# Revit family: Hager-Orion_Plus-IP65-D250-Cl.I-Steel_encl-630A-NoHosted-BE-en
name_source: partatom
category: Electrical Equipment
units: mm (PartAtom-declared; Revit-internal decimal feet)

## family parameters
Always vertical = Yes
Cut with Voids When Loaded = No
Panel Configuration = Two Columns, Circuits Across
Part Type = Panelboard
Room Calculation Point = No
Round Connector Dimension = Use Diameter
Shared = No
Work Plane-Based = Yes

## types (10) — shared parameters
Default Elevation = 1219 mm
EF000003 - Mounting method = EV000384 - Surface mounted (plaster)
EF000007 - Colour = EV000270 - Grey
EF000049 - Depth = 250 mm  [stored 0.82021 ft]
EF000116 - RAL-number = 7035
EF000118 - With mounting plate = No
EF000437 - Number of conduit inlets = 2
EF001088 - Extension possible = Yes
EF001596 - Material housing = EV000179 - Steel
EF001613 - Circuit integrity = EV000494 - None
EF004293 - Impact strength = EV008784 - IK10
EF004464 - Type of door = EV002646 - Single
EF005474 - Degree of protection (IP) = EV006421 - IP65
EF006306 - With lock = Yes
EF007800 - Suitable for lightning protection = No
EF008873 - Nominal current (In) = 630 A
EF009171 - Material plate thickness door/cover = 2 mm  [stored 0.00656168 ft]
EF009212 - Cover model = EV000116 - Closed
EF009554 - Number of openings for flange plates = 2
EF015940 - Cover with overpressure release = No
HG000002 - With door or cover = Yes
HG000003 - Range = Orion Plus
HG000006 - Flush mounted = No
HG000009 - Double swing door = No
HG000010 - Asymmetric doors = No
HG000023 - Double section enclosure = No
HG000024 - Bottom section height = 600 mm
HG000026 - Floor standing = No
Manufacturer = Hager
Type Comments = Orion Plus
zero-valued in all types: EF000218 - Built-in depth, HG000027 - Plinth height

## per-type parameters (varying)
| type | EF000008 - Width | EF000040 - Height | EF000266 - Number of rows | EF000339 - Type of cover | EF001131 - Internal depth | EF002950 - Width in number of modular spacings | EF003532 - Suitable for outdoor use | EF004427 - Number of modules | EF006244 - Transparent cover/door | EF009170 - Material plate thickness cabinet | HG000004 - Manufacturer reference |
| Surface mounted (plaster) IP65 W400 H650 D250  - FL118A | 400 mm  [stored 1.31234 ft] | 650 mm  [stored 2.13255 ft] | 4 | EV004216 - Door | 245 mm  [stored 0.803806 ft] | 16 | No | 72 | No | 2 mm  [stored 0.00656168 ft] | FL118A |
| Surface mounted (plaster) IP65 W400 H650 D250  - FL168A | 400 mm  [stored 1.31234 ft] | 650 mm  [stored 2.13255 ft] | 4 | EV004216 - Door | 245 mm  [stored 0.803806 ft] | 16 | Yes | 72 | Yes | 1 mm  [stored 0.00328084 ft] | FL168A |
| Surface mounted (plaster) IP65 W500 H650 D250  - FL120A | 500 mm  [stored 1.64042 ft] | 650 mm  [stored 2.13255 ft] | 4 | EV001012 - Cover | 250 mm  [stored 0.82021 ft] | 22 | No | 88 | No | 2 mm  [stored 0.00656168 ft] | FL120A |
| Surface mounted (plaster) IP65 W500 H650 D250  - FL170A | 500 mm  [stored 1.64042 ft] | 650 mm  [stored 2.13255 ft] | 4 | EV004216 - Door | 200 mm  [stored 0.656168 ft] | 22 | Yes | 88 | Yes | 1 mm  [stored 0.00328084 ft] | FL170A |
| Surface mounted (plaster) IP65 W600 H800 D250  - FL123A | 600 mm | 800 mm  [stored 2.62467 ft] | 5 | EV001012 - Cover | 250 mm  [stored 0.82021 ft] | 26 | No | 130 | No | 2 mm  [stored 0.00656168 ft] | FL123A |
| Surface mounted (plaster) IP65 W600 H800 D250  - FL173A | 600 mm | 800 mm  [stored 2.62467 ft] | 5 | EV004216 - Door | 250 mm  [stored 0.82021 ft] | 26 | No | 130 | Yes | 1 mm  [stored 0.00328084 ft] | FL173A |
| Surface mounted (plaster) IP65 W600 H950 D250  - FL125A | 600 mm | 950 mm  [stored 3.1168 ft] | 6 | EV001012 - Cover | 250 mm  [stored 0.82021 ft] | 26 | No | 156 | No | 2 mm  [stored 0.00656168 ft] | FL125A |
| Surface mounted (plaster) IP65 W600 H950 D250  - FL175A | 600 mm | 950 mm  [stored 3.1168 ft] | 6 | EV004216 - Door | 250 mm  [stored 0.82021 ft] | 26 | No | 156 | Yes | 1 mm  [stored 0.00328084 ft] | FL175A |
| Surface mounted (plaster) IP65 W800 H950 D250  - FL127A | 800 mm  [stored 2.62467 ft] | 950 mm  [stored 3.1168 ft] | 6 | EV001012 - Cover | 250 mm  [stored 0.82021 ft] | 37 | No | 222 | No | 2 mm  [stored 0.00656168 ft] | FL127A |
| Surface mounted (plaster) IP65 W800 H950 D250  - FL177A | 800 mm  [stored 2.62467 ft] | 950 mm  [stored 3.1168 ft] | 6 | EV004216 - Door | 250 mm  [stored 0.82021 ft] | 37 | No | 222 | Yes | 1 mm  [stored 0.00328084 ft] | FL177A |

note: [stored X ft] marks values corroborated as IEEE doubles in the binary element streams (Revit-internal decimal feet)

## geometry (parser evidence)
native form markers: Blend x4, Sweep x10
no freeform markers — native parametric forms only
